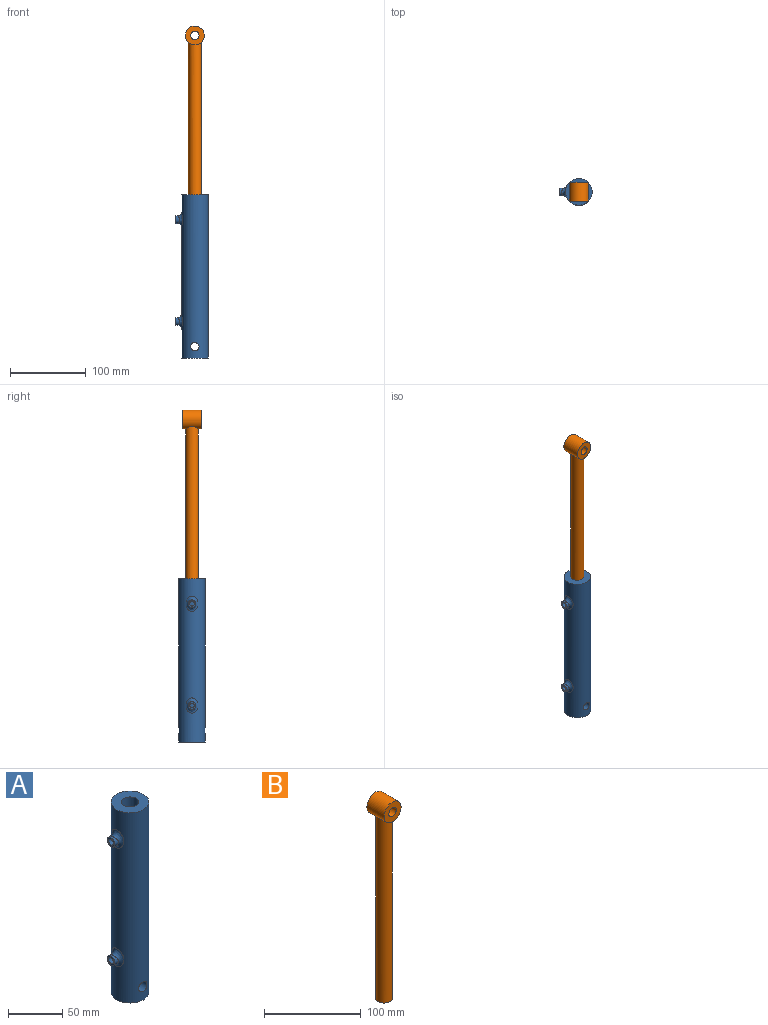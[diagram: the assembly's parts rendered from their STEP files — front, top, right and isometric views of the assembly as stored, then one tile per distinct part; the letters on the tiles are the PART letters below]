
ASSEMBLY  parts=2 mates=2
PART A: 16 faces, bbox 42.5x35x215 mm
  f0: cylinder r=17.5mm len=215mm, axis (0,0,-1), area 22946.1mm2, adj f1,f2,f3,f14,f15
  f1: plane 35x35mm, normal (0,0,1), area 761.1mm2, adj f0,f4
  f2: plane 35x35mm, normal (0,0,-1), area 962.1mm2, adj f0
  f3: cylinder r=5.5mm len=35mm, axis (0,-1,0), area 1179.1mm2, adj f0
  f4: cylinder r=8mm len=183mm, axis (0,0,1), area 9198.6mm2, adj f1,f5
  f5: plane 16x16mm, normal (0,0,1), area 201.1mm2, adj f4
  f6: plane 10x10mm, normal (-1,0,0), area 46.9mm2, adj f7,f8
  f7: cylinder r=5mm len=10mm, axis (-1,0,0), area 114.9mm2, adj f6,f15
  f8: cylinder r=3.17mm len=7.79mm, axis (-1,0,0), area 152.5mm2, adj f6,f9
  f9: cylinder r=17.5mm len=6.35mm, axis (0,0,-1), area 31.8mm2, adj f8
  f10: plane 10x10mm, normal (-1,0,0), area 46.9mm2, adj f11,f12
  f11: cylinder r=5mm len=10mm, axis (-1,0,0), area 114.9mm2, adj f10,f14
  f12: cylinder r=3.17mm len=7.79mm, axis (-1,0,0), area 152.5mm2, adj f10,f13
  f13: cylinder r=17.5mm len=6.35mm, axis (0,0,-1), area 31.8mm2, adj f12
  f14: bspline ~20.02x15.58mm, area 270.7mm2, adj f0,f11
  f15: bspline ~20.02x15.58mm, area 270.7mm2, adj f0,f7
PART B: 6 faces, bbox 25x25x255 mm
  f0: cylinder r=8.5mm len=233.34mm, axis (0,0,-1), area 12369.2mm2, adj f1,f2
  f1: plane 17x17mm, normal (0,0,-1), area 227mm2, adj f0
  f2: cylinder r=12.5mm len=25mm, axis (0,1,0), area 1720.3mm2, adj f0,f4,f5
  f3: cylinder r=5.5mm len=25mm, axis (0,1,0), area 863.9mm2, adj f4,f5
  f4: plane 25x25mm, normal (0,-1,0), area 395.8mm2, adj f2,f3
  f5: plane 25x25mm, normal (0,1,0), area 395.8mm2, adj f2,f3
PLACE A t=(-228.13,2.97,94.52)mm fixed
PLACE B t=(-228.13,2.97,61.52)mm
MATE parallel A.f4 <-> B.f0  axis (0,0,1) through (-228.13,2.97,126.52)mm
MATE slider A.f4 <-> B.f0  axis (0,0,1) through (-228.13,2.97,218.02)mm
